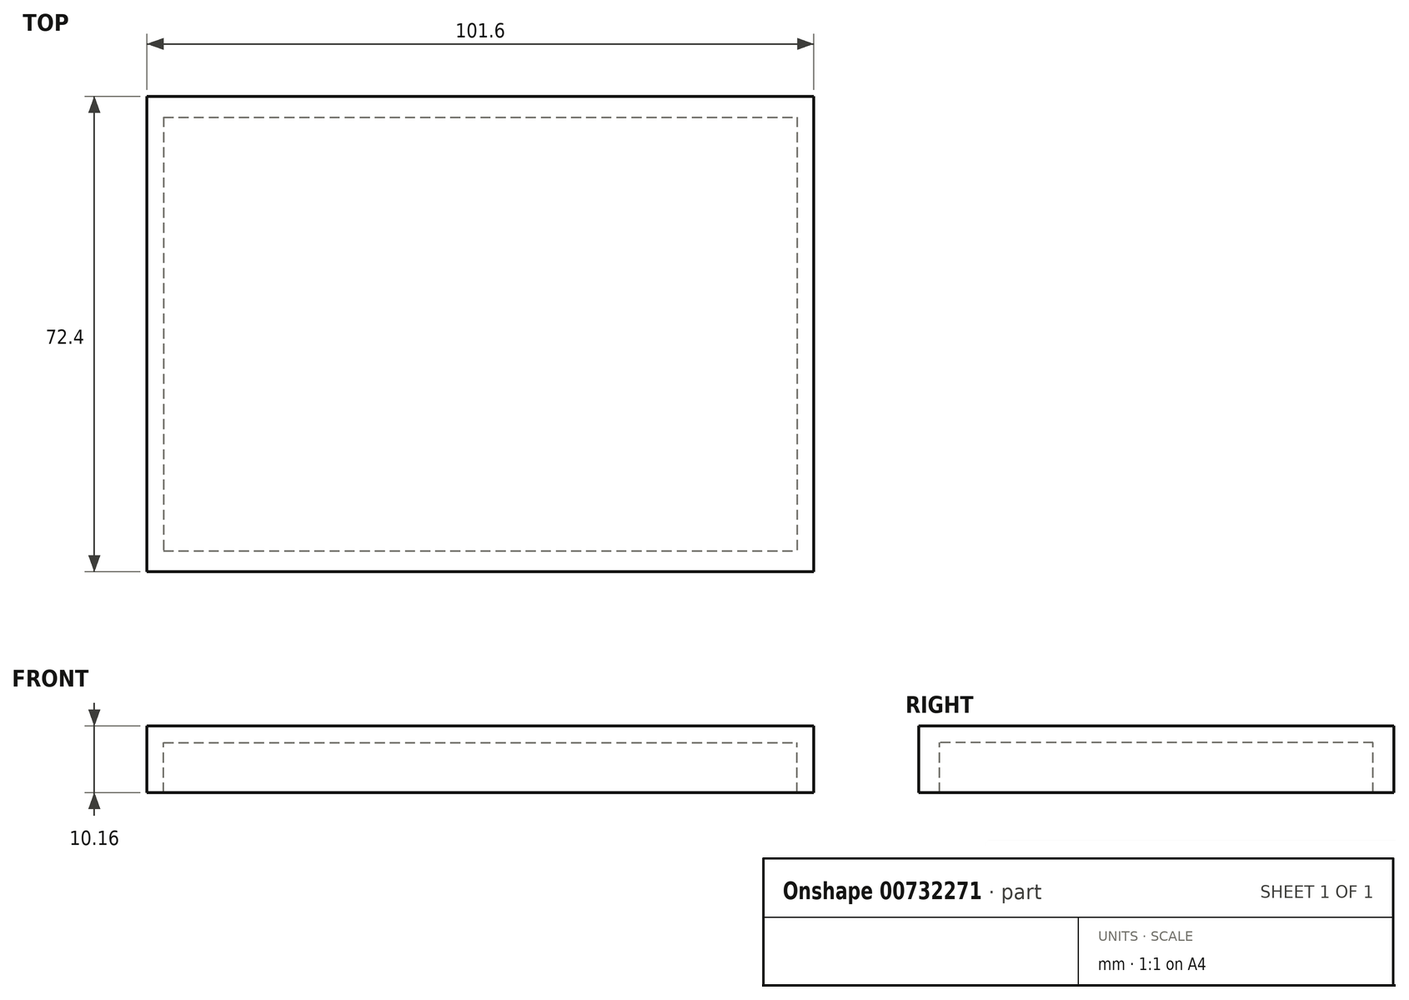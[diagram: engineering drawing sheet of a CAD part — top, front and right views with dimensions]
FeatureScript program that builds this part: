
annotation { "Feature Type Name" : "Feature", "Feature Type Description" : "" }
export const myFeature = defineFeature(function(context is Context, id is Id, definition is map)
    precondition{}
    {
        {
            var Q0;
            Q0=qCreatedBy(makeId("Top.planeOp"),FACE);
            var sketch = newSketch(context, id + "F0", { "sketchPlane" : qUnion([Q0])});
            skLineSegment(sketch, "E0.bottom", {"start": v(-48.26, 33.02) * mm, "end": v(48.26, 33.02) * mm});
            skLineSegment(sketch, "E0.top", {"start": v(-48.26, -33.02) * mm, "end": v(48.26, -33.02) * mm});
            skLineSegment(sketch, "E0.left", {"start": v(-48.26, 33.02) * mm, "end": v(-48.26, -33.02) * mm});
            skLineSegment(sketch, "E0.right", {"start": v(48.26, 33.02) * mm, "end": v(48.26, -33.02) * mm});
            skPoint(sketch, "E0.middle", {"position": v(0, 0) * mm});
            skLineSegment(sketch, "E1.bottom", {"start": v(-50.8, 36.2) * mm, "end": v(50.8, 36.2) * mm});
            skLineSegment(sketch, "E1.top", {"start": v(-50.8, -36.2) * mm, "end": v(50.8, -36.2) * mm});
            skLineSegment(sketch, "E1.left", {"start": v(-50.8, 36.2) * mm, "end": v(-50.8, -36.2) * mm});
            skLineSegment(sketch, "E1.right", {"start": v(50.8, 36.2) * mm, "end": v(50.8, -36.2) * mm});
            skSolve(sketch);
        }
        {
            var Q0;
            Q0=makeQuery(id+"F0.imprint","IMPRINT",FACE,{"disambiguationData":[TD([[makeQuery(id+"F0.imprint","IMPRINT",EDGE,{"derivedFrom":sQuery(id+"F0.wireOp",EDGE,"E0.bottom")}),-1.0]])]});
            extrude(context, id + "F1", {"entities" : qUnion([Q0]), "oppositeDirection" : true, "depth" : 2.54 * mm, "offsetDistance" : 25.4 * mm});
        }
        {
            var Q0;
            Q0 = qSketchRegion(id + "F0", true);
            extrude(context, id + "F2", {"entities" : qUnion([Q0]), "operationType" : NewBodyOperationType.ADD, "oppositeDirection" : true, "depth" : 10.16 * mm, "offsetDistance" : 25.4 * mm});
        }
    });
